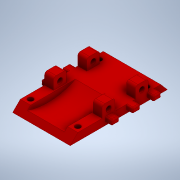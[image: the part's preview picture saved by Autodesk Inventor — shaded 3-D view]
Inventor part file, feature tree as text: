
AUTODESK INVENTOR PART (.ipt)
format: ipt  version: 2020 (Build 240168000, 168)  size: 475,136 bytes
history: native  units: mm
features: extrude x6, sketch x5, fillet x2, other x1, mirror x1, projected_geometry x1
ambient origin geometry x8: Origin, YZ Plane, XZ Plane, XY Plane, X Axis, Y Axis, Z Axis, Center Point
bodies: Solid1 (feature_tree)
feature tree (16):
  other  "WeaponMountBasePlateV1.ipt"
  extrude  "Extrusion4"  Depth=10.0mm
  extrude  "Extrusion5"  Depth=29.0mm
  extrude  "Extrusion3"  Depth=6.0mm
  extrude  "Extrusion6"  TaperAngle=0.0deg  [1 undecoded]
  fillet  "Fillet2"  Radius=4.0mm
  extrude  "Extrusion7"  Depth=4.0mm
  extrude  "Extrusion8"  Depth=6.0mm
  mirror  "Mirror2"
  fillet  "Fillet3"  Radius=4.0mm
  sketch  "Sketch4"  dims[d15=19.45mm d17=29.0mm]
  sketch  "Sketch1_1"  dims[d0=10.0mm d13=98.9mm]
  sketch  "Sketch7"  dims[d18=0.0mm d25=6.0mm]
  sketch  "Sketch8"  dims[d26=45.0mm d27=0.0mm d28=4.0mm]
  sketch  "Sketch9"  dims[d29=6.0mm d30=4.0mm d31=6.0mm d32=4.0mm d33=6.0mm d34=55.3mm d35=0.0mm d37=50.45mm d38=4.25mm d39=3.75mm d40=4.0mm d42=4.0mm d44=0.0mm d45=0.0mm d49=1.0mm d50=10.0mm d51=8.0mm d52=20.0mm d53=7.0mm d54=0.0mm d57=4.2mm d58=4.2mm d59=0.0mm d60=0.0mm d61=4.0mm d62=2.0mm d63=4.0mm d64=5.0mm d65=10.0mm d66=4.0mm d67=5.0mm d68=9.0mm d74=64.0mm]
  projected_geometry  "Projected Loop4"
note: 1 required parameter value undecoded (feature->parameter linkage not recoverable at this tier; creation-order binding heuristic only, values carry confidence <= 0.55)
